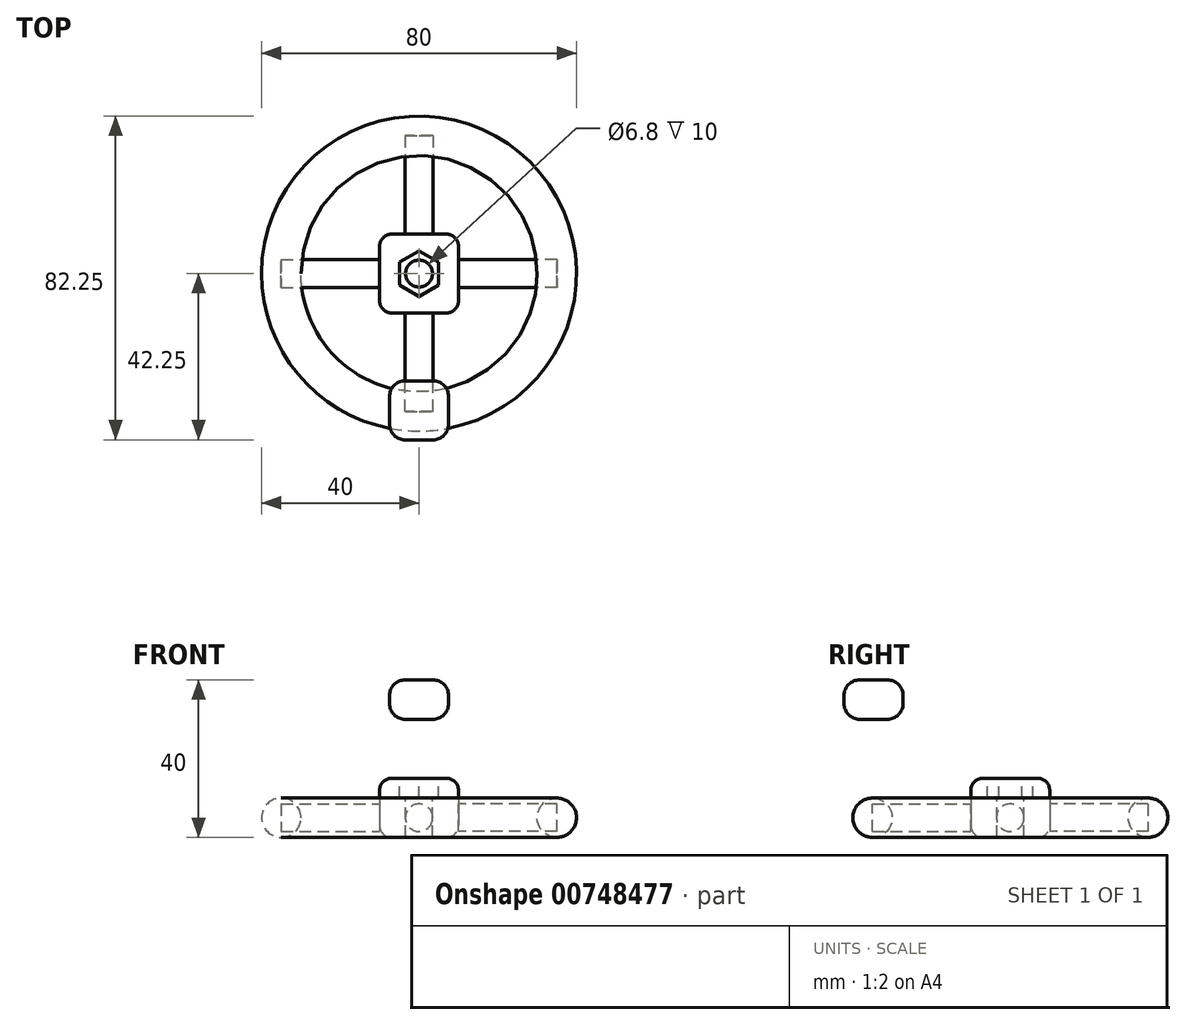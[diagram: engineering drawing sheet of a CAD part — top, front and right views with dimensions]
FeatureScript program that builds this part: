
annotation { "Feature Type Name" : "Feature", "Feature Type Description" : "" }
export const myFeature = defineFeature(function(context is Context, id is Id, definition is map)
    precondition{}
    {
        {
            var Q0;
            Q0=qCreatedBy(makeId("Front.planeOp"),FACE);
            var sketch = newSketch(context, id + "F0", { "sketchPlane" : qUnion([Q0])});
            skCircle(sketch, "E0", {"center": v(35, 0) * mm, "radius": 5 * mm});
            skSolve(sketch);
        }
        {
            var Q0;
            Q0=qCreatedBy(makeId("Top.planeOp"),FACE);
            var sketch = newSketch(context, id + "F1", { "sketchPlane" : qUnion([Q0])});
            skCircle(sketch, "E1", {"center": v(0, 0) * mm, "radius": 35 * mm});
            skSolve(sketch);
        }
        {
            var Q0;
            Q0=makeQuery(id+"F0.imprint","IMPRINT",FACE,{"disambiguationData":[TD([[makeQuery(id+"F0.imprint","IMPRINT",EDGE,{"derivedFrom":sQuery(id+"F0.wireOp",EDGE,"E0")}),1.0]])]});
            var Q1;
            Q1=sQuery(id+"F1.wireOp",EDGE,"E1");
            revolve(context, id + "F2", {"surfaceOperationType" : NewSurfaceOperationType.NEW, "entities" : qUnion([Q0]), "axis" : qUnion([Q1]), "revolveType" : RevolveType.FULL});
        }
        {
            var Q0;
            Q0=qCreatedBy(makeId("Top.planeOp"),FACE);
            var sketch = newSketch(context, id + "F3", { "sketchPlane" : qUnion([Q0])});
            skLineSegment(sketch, "E2.bottom", {"start": v(10, -10) * mm, "end": v(-10, -10) * mm});
            skLineSegment(sketch, "E2.top", {"start": v(10, 10) * mm, "end": v(-10, 10) * mm});
            skLineSegment(sketch, "E2.left", {"start": v(10, -10) * mm, "end": v(10, 10) * mm});
            skLineSegment(sketch, "E2.right", {"start": v(-10, -10) * mm, "end": v(-10, 10) * mm});
            skPoint(sketch, "E2.middle", {"position": v(0, 0) * mm});
            skSolve(sketch);
        }
        {
            var Q0;
            Q0=makeQuery(id+"F3.imprint","IMPRINT",FACE,{"disambiguationData":[TD([[makeQuery(id+"F3.imprint","IMPRINT",EDGE,{"derivedFrom":sQuery(id+"F3.wireOp",EDGE,"E2.bottom")}),-1.0]])]});
            extrude(context, id + "F4", {"entities" : qUnion([Q0]), "depth" : 10 * mm, "offsetDistance" : 25 * mm, "hasSecondDirection" : true, "secondDirectionOppositeDirection" : true, "secondDirectionDepth" : 5 * mm});
        }
        {
            var Q0;
            Q0=makeQuery(id+"F4.opExtrude","CAP_EDGE",EDGE,{"disambiguationData":[OSD([sQuery(id+"F3.wireOp",EDGE,"E2.right")])],"isStart":false});
            var Q1;
            Q1=makeQuery(id+"F4.opExtrude","CAP_EDGE",EDGE,{"disambiguationData":[OSD([sQuery(id+"F3.wireOp",EDGE,"E2.bottom")])],"isStart":false});
            var Q2;
            Q2=makeQuery(id+"F4.opExtrude","CAP_EDGE",EDGE,{"disambiguationData":[OSD([sQuery(id+"F3.wireOp",EDGE,"E2.left")])],"isStart":false});
            var Q3;
            Q3=makeQuery(id+"F4.opExtrude","CAP_FACE",FACE,{"disambiguationData":[OSD([sQuery(id+"F3.wireOp",EDGE,"E2.bottom"),sQuery(id+"F3.wireOp",EDGE,"E2.top"),sQuery(id+"F3.wireOp",EDGE,"E2.left"),sQuery(id+"F3.wireOp",EDGE,"E2.right")])],"isStart":false});
            var Q4;
            Q4=makeQuery(id+"F4.opExtrude","SWEPT_EDGE",EDGE,{"disambiguationData":[OSD([sQuery(id+"F3.wireOp",EDGE,"E2.bottom"),sQuery(id+"F3.wireOp",EDGE,"E2.left")])]});
            var Q5;
            Q5=makeQuery(id+"F4.opExtrude","SWEPT_EDGE",EDGE,{"disambiguationData":[OSD([sQuery(id+"F3.wireOp",EDGE,"E2.bottom"),sQuery(id+"F3.wireOp",EDGE,"E2.right")])]});
            var Q6;
            Q6=makeQuery(id+"F4.opExtrude","SWEPT_EDGE",EDGE,{"disambiguationData":[OSD([sQuery(id+"F3.wireOp",EDGE,"E2.top"),sQuery(id+"F3.wireOp",EDGE,"E2.left")])]});
            var Q7;
            Q7=makeQuery(id+"F4.opExtrude","SWEPT_EDGE",EDGE,{"disambiguationData":[OSD([sQuery(id+"F3.wireOp",EDGE,"E2.top"),sQuery(id+"F3.wireOp",EDGE,"E2.right")])]});
            var Q8;
            Q8=makeQuery(id+"F4.opExtrude","CAP_FACE",FACE,{"disambiguationData":[OSD([sQuery(id+"F3.wireOp",EDGE,"E2.bottom"),sQuery(id+"F3.wireOp",EDGE,"E2.top"),sQuery(id+"F3.wireOp",EDGE,"E2.left"),sQuery(id+"F3.wireOp",EDGE,"E2.right")])],"isStart":true});
            fillet(context, id + "F5", {"entities" : qUnion([Q0, Q1, Q2, Q3, Q4, Q5, Q6, Q7, Q8]), "radius" : 3 * mm, "tangentPropagation" : true, "allowEdgeOverflow" : false});
        }
        {
            var Q0;
            Q0=makeQuery(id+"F4.opExtrude","CAP_FACE",FACE,{"disambiguationData":[OSD([sQuery(id+"F3.wireOp",EDGE,"E2.bottom"),sQuery(id+"F3.wireOp",EDGE,"E2.top"),sQuery(id+"F3.wireOp",EDGE,"E2.left"),sQuery(id+"F3.wireOp",EDGE,"E2.right")])],"isStart":false});
            var sketch = newSketch(context, id + "F6", { "sketchPlane" : qUnion([Q0])});
            skCircle(sketch, "E3.cCircle", {"center": v(0, 0) * mm, "radius": 5 * mm, "construction": true});
            skLineSegment(sketch, "E3.0", {"start": v(5, -2.89) * mm, "end": v(0, -5.77) * mm});
            skLineSegment(sketch, "E3.1", {"start": v(0, -5.77) * mm, "end": v(-5, -2.89) * mm});
            skLineSegment(sketch, "E3.2", {"start": v(-5, -2.89) * mm, "end": v(-5, 2.89) * mm});
            skLineSegment(sketch, "E3.3", {"start": v(-5, 2.89) * mm, "end": v(0, 5.77) * mm});
            skLineSegment(sketch, "E3.4", {"start": v(0, 5.77) * mm, "end": v(5, 2.89) * mm});
            skLineSegment(sketch, "E3.5", {"start": v(5, 2.89) * mm, "end": v(5, -2.89) * mm});
            skPoint(sketch, "E3.0.midPoint", {"position": v(2.5, -4.33) * mm});
            skSolve(sketch);
        }
        {
            var Q0;
            Q0=makeQuery(id+"F6.imprint","IMPRINT",FACE,{"disambiguationData":[TD([[makeQuery(id+"F6.imprint","IMPRINT",EDGE,{"derivedFrom":sQuery(id+"F6.wireOp",EDGE,"E3.0")}),-1.0]])]});
            extrude(context, id + "F7", {"entities" : qUnion([Q0]), "operationType" : NewBodyOperationType.REMOVE, "oppositeDirection" : true, "depth" : 5 * mm, "offsetDistance" : 25 * mm});
        }
        {
            var Q0;
            Q0=makeQuery(id+"F7.boolean.opBoolean","COPY",FACE,{"derivedFrom":makeQuery(id+"F7.opExtrude","CAP_FACE",FACE,{"disambiguationData":[OSD([sQuery(id+"F6.wireOp",EDGE,"E3.0"),sQuery(id+"F6.wireOp",EDGE,"E3.1"),sQuery(id+"F6.wireOp",EDGE,"E3.2"),sQuery(id+"F6.wireOp",EDGE,"E3.3"),sQuery(id+"F6.wireOp",EDGE,"E3.4"),sQuery(id+"F6.wireOp",EDGE,"E3.5")])],"isStart":false})});
            var sketch = newSketch(context, id + "F8", { "sketchPlane" : qUnion([Q0])});
            skCircle(sketch, "E4", {"center": v(0, 0) * mm, "radius": 3.4 * mm});
            skSolve(sketch);
        }
        {
            var Q0;
            Q0=makeQuery(id+"F8.imprint","IMPRINT",FACE,{"disambiguationData":[TD([[makeQuery(id+"F8.imprint","IMPRINT",EDGE,{"derivedFrom":sQuery(id+"F8.wireOp",EDGE,"E4")}),1.0]])]});
            extrude(context, id + "F9", {"entities" : qUnion([Q0]), "operationType" : NewBodyOperationType.REMOVE, "endBound" : BoundingType.THROUGH_ALL, "oppositeDirection" : true, "depth" : 25 * mm, "offsetDistance" : 25 * mm});
        }
        {
            var Q0;
            Q0=makeQuery(id+"F4.opExtrude","SWEPT_FACE",FACE,{"disambiguationData":[OSD([sQuery(id+"F3.wireOp",EDGE,"E2.left")])]});
            var sketch = newSketch(context, id + "F10", { "sketchPlane" : qUnion([Q0])});
            skCircle(sketch, "E5", {"center": v(0, 0) * mm, "radius": 3.5 * mm});
            skSolve(sketch);
        }
        {
            var Q0;
            Q0=makeQuery(id+"F10.imprint","IMPRINT",FACE,{"disambiguationData":[TD([[makeQuery(id+"F10.imprint","IMPRINT",EDGE,{"derivedFrom":sQuery(id+"F10.wireOp",EDGE,"E5")}),1.0]])]});
            extrude(context, id + "F11", {"entities" : qUnion([Q0]), "depth" : 25 * mm, "offsetDistance" : 25 * mm});
        }
        {
            var Q0;
            Q0=makeQuery(id+"F4.opExtrude","SWEPT_FACE",FACE,{"disambiguationData":[OSD([sQuery(id+"F3.wireOp",EDGE,"E2.right")])]});
            var sketch = newSketch(context, id + "F12", { "sketchPlane" : qUnion([Q0])});
            skCircle(sketch, "E6", {"center": v(0, 0) * mm, "radius": 3.5 * mm});
            skSolve(sketch);
        }
        {
            var Q0;
            Q0=makeQuery(id+"F12.imprint","IMPRINT",FACE,{"disambiguationData":[TD([[makeQuery(id+"F12.imprint","IMPRINT",EDGE,{"derivedFrom":sQuery(id+"F12.wireOp",EDGE,"E6")}),1.0]])]});
            var Q1;
            Q1=sQuery(id+"F12.wireOp",EDGE,"E6");
            extrude(context, id + "F13", {"entities" : qUnion([Q0]), "surfaceOperationType" : NewSurfaceOperationType.ADD, "surfaceEntities" : qUnion([Q1]), "depth" : 25 * mm, "offsetDistance" : 25 * mm});
        }
        {
            var Q0;
            Q0=makeQuery(id+"F4.opExtrude","SWEPT_FACE",FACE,{"disambiguationData":[OSD([sQuery(id+"F3.wireOp",EDGE,"E2.top")])]});
            var sketch = newSketch(context, id + "F14", { "sketchPlane" : qUnion([Q0])});
            skCircle(sketch, "E7", {"center": v(0, 0) * mm, "radius": 3.5 * mm});
            skSolve(sketch);
        }
        {
            var Q0;
            Q0=makeQuery(id+"F14.imprint","IMPRINT",FACE,{"disambiguationData":[TD([[makeQuery(id+"F14.imprint","IMPRINT",EDGE,{"derivedFrom":sQuery(id+"F14.wireOp",EDGE,"E7")}),1.0]])]});
            var Q1;
            Q1=sQuery(id+"F14.wireOp",EDGE,"E7");
            extrude(context, id + "F15", {"entities" : qUnion([Q0]), "surfaceEntities" : qUnion([Q1]), "depth" : 25 * mm, "offsetDistance" : 25 * mm});
        }
        {
            var Q0;
            Q0=makeQuery(id+"F4.opExtrude","SWEPT_FACE",FACE,{"disambiguationData":[OSD([sQuery(id+"F3.wireOp",EDGE,"E2.bottom")])]});
            var sketch = newSketch(context, id + "F16", { "sketchPlane" : qUnion([Q0])});
            skCircle(sketch, "E8", {"center": v(0, 0) * mm, "radius": 3.5 * mm});
            skSolve(sketch);
        }
        {
            var Q0;
            Q0=makeQuery(id+"F16.imprint","IMPRINT",FACE,{"disambiguationData":[TD([[makeQuery(id+"F16.imprint","IMPRINT",EDGE,{"derivedFrom":sQuery(id+"F16.wireOp",EDGE,"E8")}),1.0]])]});
            var Q1;
            Q1=sQuery(id+"F16.wireOp",EDGE,"E8");
            extrude(context, id + "F17", {"entities" : qUnion([Q0]), "surfaceEntities" : qUnion([Q1]), "depth" : 25 * mm, "offsetDistance" : 25 * mm});
        }
        {
            var Q0;
            Q0=qCreatedBy(makeId("Top.planeOp"),FACE);
            var sketch = newSketch(context, id + "F18", { "sketchPlane" : qUnion([Q0])});
            skCircle(sketch, "E9", {"center": v(0, -34.18) * mm, "radius": 4 * mm});
            skSolve(sketch);
        }
        {
            var Q0;
            Q0=sQuery(id+"F18.wireOp",EDGE,"E9");
            extrude(context, id + "F19", {"bodyType" : ToolBodyType.SURFACE, "surfaceEntities" : qUnion([Q0]), "depth" : 30 * mm, "offsetDistance" : 25 * mm});
        }
        {
            var Q0;
            Q0=qCreatedBy(makeId("Top.planeOp"),FACE);
            cPlane(context, id + "F20", {"entities" : qUnion([Q0]), "cplaneType" : CPlaneType.OFFSET, "offset" : 30 * mm, "width" : 150 * mm, "height" : 150 * mm});
        }
        {
            var Q0;
            Q0=qCreatedBy(id+"F20.planeOp",FACE);
            var sketch = newSketch(context, id + "F21", { "sketchPlane" : qUnion([Q0])});
            skLineSegment(sketch, "E10.bottom", {"start": v(7.5, -42.25) * mm, "end": v(-7.5, -42.25) * mm});
            skLineSegment(sketch, "E10.top", {"start": v(7.5, -27.25) * mm, "end": v(-7.5, -27.25) * mm});
            skLineSegment(sketch, "E10.left", {"start": v(7.5, -42.25) * mm, "end": v(7.5, -27.25) * mm});
            skLineSegment(sketch, "E10.right", {"start": v(-7.5, -42.25) * mm, "end": v(-7.5, -27.25) * mm});
            skPoint(sketch, "E10.middle", {"position": v(0, -34.75) * mm});
            skSolve(sketch);
        }
        {
            var Q0;
            Q0=makeQuery(id+"F21.imprint","IMPRINT",FACE,{"disambiguationData":[TD([[makeQuery(id+"F21.imprint","IMPRINT",EDGE,{"derivedFrom":sQuery(id+"F21.wireOp",EDGE,"E10.bottom")}),-1.0]])]});
            extrude(context, id + "F22", {"entities" : qUnion([Q0]), "depth" : 5 * mm, "offsetDistance" : 25 * mm, "hasSecondDirection" : true, "secondDirectionOppositeDirection" : true, "secondDirectionDepth" : 5 * mm});
        }
        {
            var Q0;
            Q0=makeQuery(id+"F22.opExtrude","CAP_EDGE",EDGE,{"disambiguationData":[OSD([sQuery(id+"F21.wireOp",EDGE,"E10.right")])],"isStart":false});
            var Q1;
            Q1=makeQuery(id+"F22.opExtrude","CAP_EDGE",EDGE,{"disambiguationData":[OSD([sQuery(id+"F21.wireOp",EDGE,"E10.bottom")])],"isStart":false});
            var Q2;
            Q2=makeQuery(id+"F22.opExtrude","CAP_EDGE",EDGE,{"disambiguationData":[OSD([sQuery(id+"F21.wireOp",EDGE,"E10.left")])],"isStart":false});
            var Q3;
            Q3=makeQuery(id+"F22.opExtrude","CAP_FACE",FACE,{"disambiguationData":[OSD([sQuery(id+"F21.wireOp",EDGE,"E10.bottom"),sQuery(id+"F21.wireOp",EDGE,"E10.top"),sQuery(id+"F21.wireOp",EDGE,"E10.left"),sQuery(id+"F21.wireOp",EDGE,"E10.right")])],"isStart":false});
            var Q4;
            Q4=makeQuery(id+"F22.opExtrude","CAP_EDGE",EDGE,{"disambiguationData":[OSD([sQuery(id+"F21.wireOp",EDGE,"E10.bottom")])],"isStart":true});
            var Q5;
            Q5=makeQuery(id+"F22.opExtrude","CAP_EDGE",EDGE,{"disambiguationData":[OSD([sQuery(id+"F21.wireOp",EDGE,"E10.right")])],"isStart":true});
            var Q6;
            Q6=makeQuery(id+"F22.opExtrude","CAP_EDGE",EDGE,{"disambiguationData":[OSD([sQuery(id+"F21.wireOp",EDGE,"E10.left")])],"isStart":true});
            var Q7;
            Q7=makeQuery(id+"F22.opExtrude","CAP_EDGE",EDGE,{"disambiguationData":[OSD([sQuery(id+"F21.wireOp",EDGE,"E10.top")])],"isStart":true});
            var Q8;
            Q8=makeQuery(id+"F22.opExtrude","SWEPT_EDGE",EDGE,{"disambiguationData":[OSD([sQuery(id+"F21.wireOp",EDGE,"E10.bottom"),sQuery(id+"F21.wireOp",EDGE,"E10.right")])]});
            var Q9;
            Q9=makeQuery(id+"F22.opExtrude","SWEPT_EDGE",EDGE,{"disambiguationData":[OSD([sQuery(id+"F21.wireOp",EDGE,"E10.bottom"),sQuery(id+"F21.wireOp",EDGE,"E10.left")])]});
            var Q10;
            Q10=makeQuery(id+"F22.opExtrude","SWEPT_EDGE",EDGE,{"disambiguationData":[OSD([sQuery(id+"F21.wireOp",EDGE,"E10.top"),sQuery(id+"F21.wireOp",EDGE,"E10.left")])]});
            var Q11;
            Q11=makeQuery(id+"F22.opExtrude","SWEPT_EDGE",EDGE,{"disambiguationData":[OSD([sQuery(id+"F21.wireOp",EDGE,"E10.top"),sQuery(id+"F21.wireOp",EDGE,"E10.right")])]});
            fillet(context, id + "F23", {"entities" : qUnion([Q0, Q1, Q2, Q3, Q4, Q5, Q6, Q7, Q8, Q9, Q10, Q11]), "radius" : 4 * mm, "tangentPropagation" : true, "allowEdgeOverflow" : false});
        }
    });
